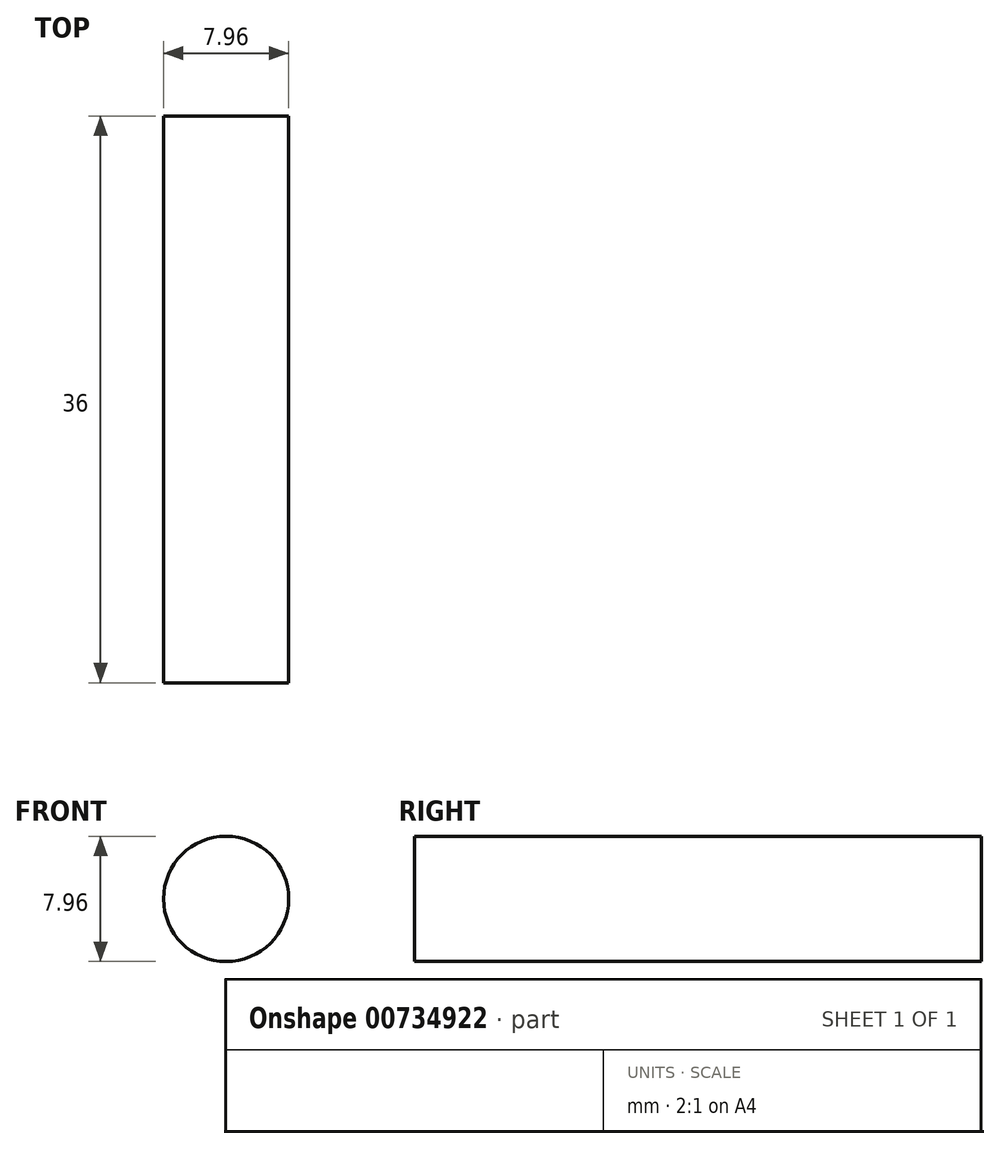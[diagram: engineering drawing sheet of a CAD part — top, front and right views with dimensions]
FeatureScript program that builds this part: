
annotation { "Feature Type Name" : "Feature", "Feature Type Description" : "" }
export const myFeature = defineFeature(function(context is Context, id is Id, definition is map)
    precondition{}
    {
        {
            var Q0;
            Q0=qCreatedBy(makeId("Front.planeOp"),FACE);
            var sketch = newSketch(context, id + "F0", { "sketchPlane" : qUnion([Q0])});
            skCircle(sketch, "E0", {"center": v(0, 0) * mm, "radius": 3.98 * mm});
            skSolve(sketch);
        }
        {
            var Q0;
            Q0 = qSketchRegion(id + "F0", true);
            extrude(context, id + "F1", {"entities" : qUnion([Q0]), "depth" : 36 * mm, "offsetDistance" : 25 * mm});
        }
    });
